# Revit family: Krowne_11-400L-W_DeckMount_Faucet
name_source: partatom
category: Plumbing Fixtures
revit_build: Autodesk Revit 2018 (Build: 20181015_0930(x64)
units: mm (PartAtom-declared; Revit-internal decimal feet)

## family parameters
Always vertical = Yes
Cut with Voids When Loaded = No
OmniClass Number = 23.40.40.00
OmniClass Title = Food Service Equipment and Furnishings
Part Type = Normal
Room Calculation Point = No
Round Connector Dimension = Use Diameter
Shared = No
Work Plane-Based = No

## types (1)
- 11-400L-W
    Assembly Code = E1090300
    Cold Water Connection Height = 0"
    Cold Water Flow = 2 GPM
    Cold Water Size = 1"
    Depth = 3 1/2"
    Description = Silver Series 4" Deck Mount Faucet with 3-1/2" Wide Gooseneck Spout & Vandal Resistant Wrist Blades Handles
    Foodservice Equipment Identifier = Yes
    Height = 8"
    Hot Water Connection Height = 0"
    Hot Water Consumption = 0 GPM
    Hot Water Flow = 2 GPM
    Hot Water Size = 1"
    Hot Water Temperature = 100 °F
    Manufacturer = Krowne Metal
    Model = 11-400L-W
    URL = https://krowne.com
    Weight in Pounds = 3
    Width = 8 3/8"

## geometry (parser evidence)
native form markers: Sweep x2
no freeform markers — native parametric forms only
